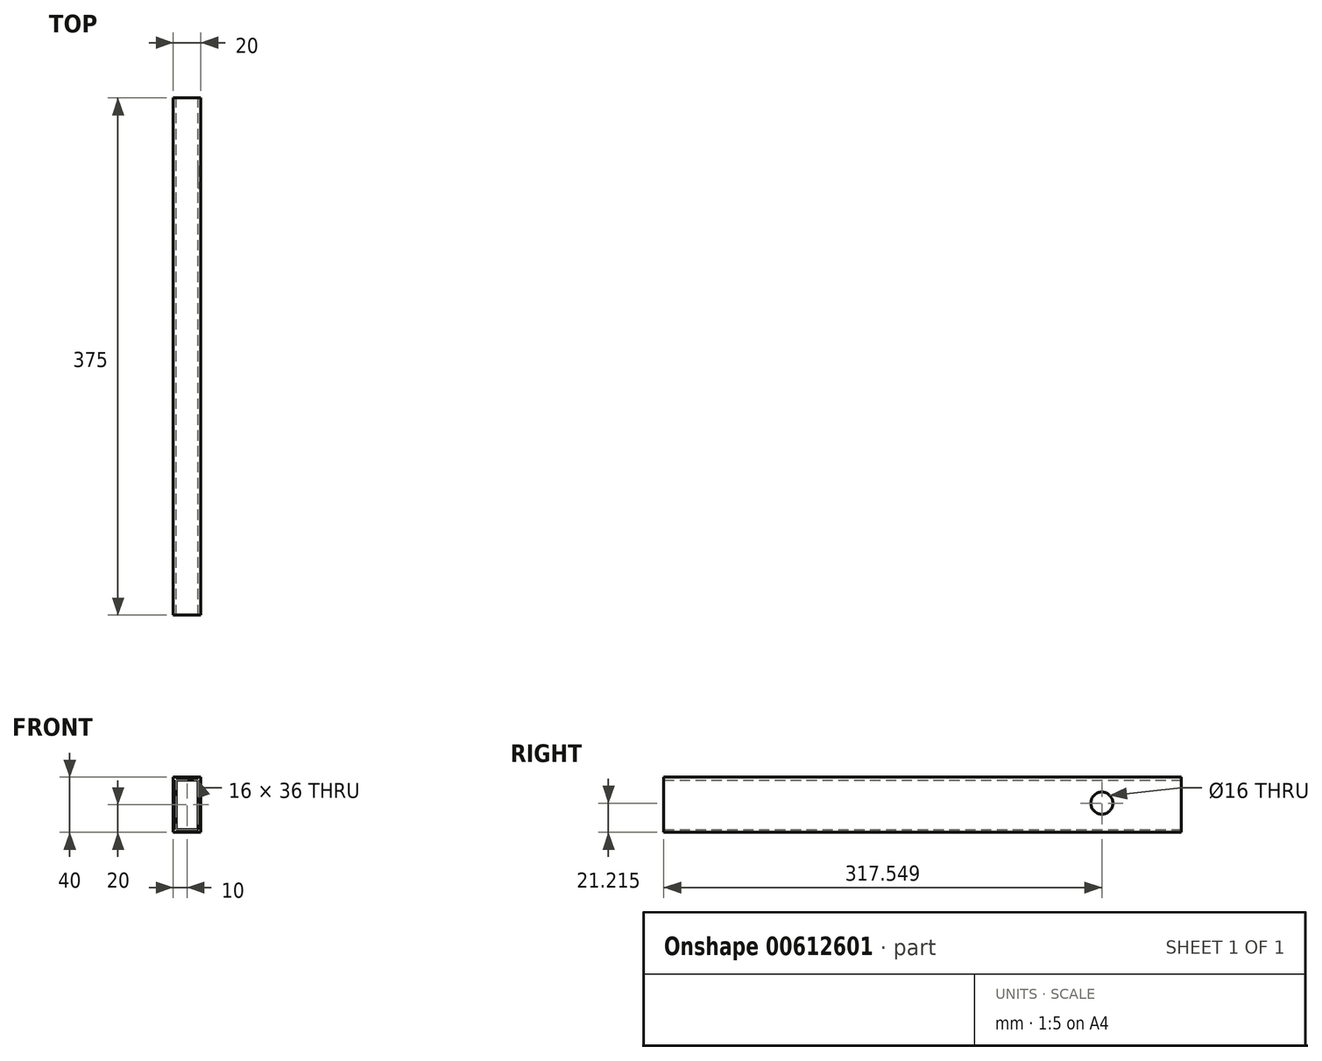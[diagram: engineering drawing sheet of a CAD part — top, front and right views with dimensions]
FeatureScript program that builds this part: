
annotation { "Feature Type Name" : "Feature", "Feature Type Description" : "" }
export const myFeature = defineFeature(function(context is Context, id is Id, definition is map)
    precondition{}
    {
        {
            var Q0;
            Q0=qCreatedBy(makeId("Front.planeOp"),FACE);
            var sketch = newSketch(context, id + "F0", { "sketchPlane" : qUnion([Q0])});
            skLineSegment(sketch, "E0.bottom", {"start": v(0, 0) * mm, "end": v(20, 0) * mm});
            skLineSegment(sketch, "E0.top", {"start": v(0, -40) * mm, "end": v(20, -40) * mm});
            skLineSegment(sketch, "E0.left", {"start": v(0, 0) * mm, "end": v(0, -40) * mm});
            skLineSegment(sketch, "E0.right", {"start": v(20, 0) * mm, "end": v(20, -40) * mm});
            skLineSegment(sketch, "E1.0", {"start": v(2, -2) * mm, "end": v(18, -2) * mm});
            skLineSegment(sketch, "E1.1", {"start": v(2, -2) * mm, "end": v(2, -38) * mm});
            skLineSegment(sketch, "E1.2", {"start": v(2, -38) * mm, "end": v(18, -38) * mm});
            skLineSegment(sketch, "E1.3", {"start": v(18, -2) * mm, "end": v(18, -38) * mm});
            skSolve(sketch);
        }
        {
            var Q0;
            Q0=makeQuery(id+"F0.imprint","IMPRINT",FACE,{"disambiguationData":[TD([[makeQuery(id+"F0.imprint","IMPRINT",EDGE,{"derivedFrom":sQuery(id+"F0.wireOp",EDGE,"E0.bottom")}),-1.0]])]});
            extrude(context, id + "F1", {"entities" : qUnion([Q0]), "depth" : 375 * mm, "offsetDistance" : 25.4 * mm});
        }
        {
            var Q0;
            Q0=makeQuery(id+"F1.opExtrude","SWEPT_FACE",FACE,{"disambiguationData":[OSD([sQuery(id+"F0.wireOp",EDGE,"E0.right")])]});
            var sketch = newSketch(context, id + "F2", { "sketchPlane" : qUnion([Q0])});
            skCircle(sketch, "E2", {"center": v(-57.45, -18.79) * mm, "radius": 8 * mm});
            skSolve(sketch);
        }
        {
            var Q0;
            Q0=makeQuery(id+"F2.imprint","IMPRINT",FACE,{"disambiguationData":[TD([[makeQuery(id+"F2.imprint","IMPRINT",EDGE,{"derivedFrom":sQuery(id+"F2.wireOp",EDGE,"E2")}),1.0]])]});
            extrude(context, id + "F3", {"entities" : qUnion([Q0]), "operationType" : NewBodyOperationType.REMOVE, "oppositeDirection" : true, "depth" : 15 * mm, "offsetDistance" : 25.4 * mm});
        }
    });
